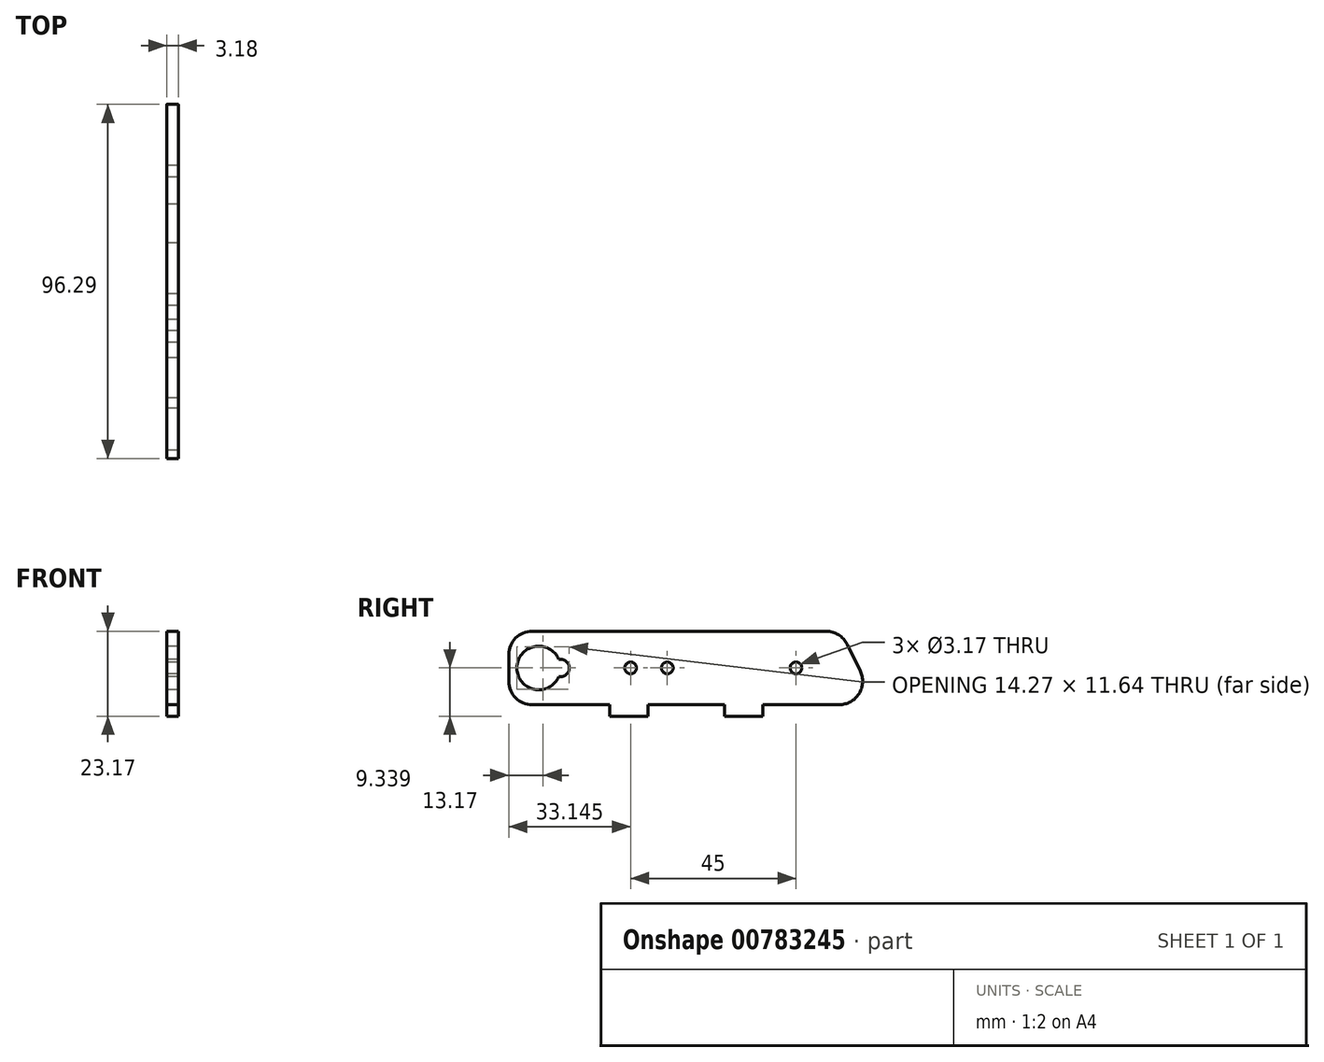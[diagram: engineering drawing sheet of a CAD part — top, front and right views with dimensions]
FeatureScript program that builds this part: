
annotation { "Feature Type Name" : "Feature", "Feature Type Description" : "" }
export const myFeature = defineFeature(function(context is Context, id is Id, definition is map)
    precondition{}
    {
        {
            var Q0;
            Q0=qCreatedBy(makeId("Right.planeOp"),FACE);
            var sketch = newSketch(context, id + "F0", { "sketchPlane" : qUnion([Q0])});
            skLineSegment(sketch, "E0", {"start": v(-32.28, 0) * mm, "end": v(-32.03, 0) * mm});
            skArc(sketch, "E1.filletArc", {"start": v(-38.63, 6.35) * mm, "mid": v(-36.77, 1.86) * mm, "end": v(-32.28, 0) * mm});
            skArc(sketch, "E2.filletArc", {"start": v(51.3, 0) * mm, "mid": v(56.7, 2.98) * mm, "end": v(57.02, 9.13) * mm});
            skArc(sketch, "E3.filletArc", {"start": v(53.46, 16.43) * mm, "mid": v(51.12, 19.03) * mm, "end": v(47.75, 20) * mm});
            skLineSegment(sketch, "E4", {"start": v(53.46, 16.43) * mm, "end": v(57.02, 9.13) * mm});
            skLineSegment(sketch, "E5", {"start": v(-28.72, 20) * mm, "end": v(47.75, 20) * mm});
            skLineSegment(sketch, "E6.top", {"start": v(-11.2, -3.17) * mm, "end": v(-0.78, -3.17) * mm});
            skLineSegment(sketch, "E6.left", {"start": v(-11.2, 0) * mm, "end": v(-11.2, -3.17) * mm});
            skLineSegment(sketch, "E6.right", {"start": v(30.47, 0) * mm, "end": v(30.47, -3.17) * mm});
            skLineSegment(sketch, "E7", {"start": v(20.05, 0) * mm, "end": v(20.05, -3.17) * mm});
            skLineSegment(sketch, "E8", {"start": v(-0.78, 0) * mm, "end": v(-0.78, -3.17) * mm});
            skLineSegment(sketch, "E9.trimOffspring", {"start": v(20.05, -3.17) * mm, "end": v(30.47, -3.17) * mm});
            skLineSegment(sketch, "E10", {"start": v(-32.03, 0) * mm, "end": v(-11.2, 0) * mm});
            skLineSegment(sketch, "E11.trimOffspring", {"start": v(30.47, 0) * mm, "end": v(51.3, 0) * mm});
            skLineSegment(sketch, "E12.trimOffspring", {"start": v(-0.78, 0) * mm, "end": v(20.05, 0) * mm});
            skPoint(sketch, "E13.end.orphan", {"position": v(39.52, 10) * mm});
            skCircle(sketch, "E14", {"center": v(4.52, 10) * mm, "radius": 1.59 * mm});
            skCircle(sketch, "E15", {"center": v(39.52, 10) * mm, "radius": 1.59 * mm});
            skArc(sketch, "E16", {"start": v(-25.02, 12.34) * mm, "mid": v(-36.43, 10) * mm, "end": v(-25.02, 7.66) * mm});
            skArc(sketch, "E17", {"start": v(-25.02, 7.66) * mm, "mid": v(-22.15, 10) * mm, "end": v(-25.02, 12.34) * mm});
            skLineSegment(sketch, "E18.top", {"start": v(-32.28, 20) * mm, "end": v(-28.72, 20) * mm});
            skLineSegment(sketch, "E18.left", {"start": v(-38.63, 6.35) * mm, "end": v(-38.63, 13.65) * mm});
            skArc(sketch, "E19.filletArc", {"start": v(-32.28, 20) * mm, "mid": v(-36.77, 18.14) * mm, "end": v(-38.63, 13.65) * mm});
            skCircle(sketch, "E20", {"center": v(-5.48, 10) * mm, "radius": 1.59 * mm});
            skSolve(sketch);
        }
        {
            var Q0;
            Q0 = qSketchRegion(id + "F0", true);
            extrude(context, id + "F1", {"entities" : qUnion([Q0]), "depth" : 3.17 * mm, "offsetDistance" : 25.4 * mm});
        }
    });
